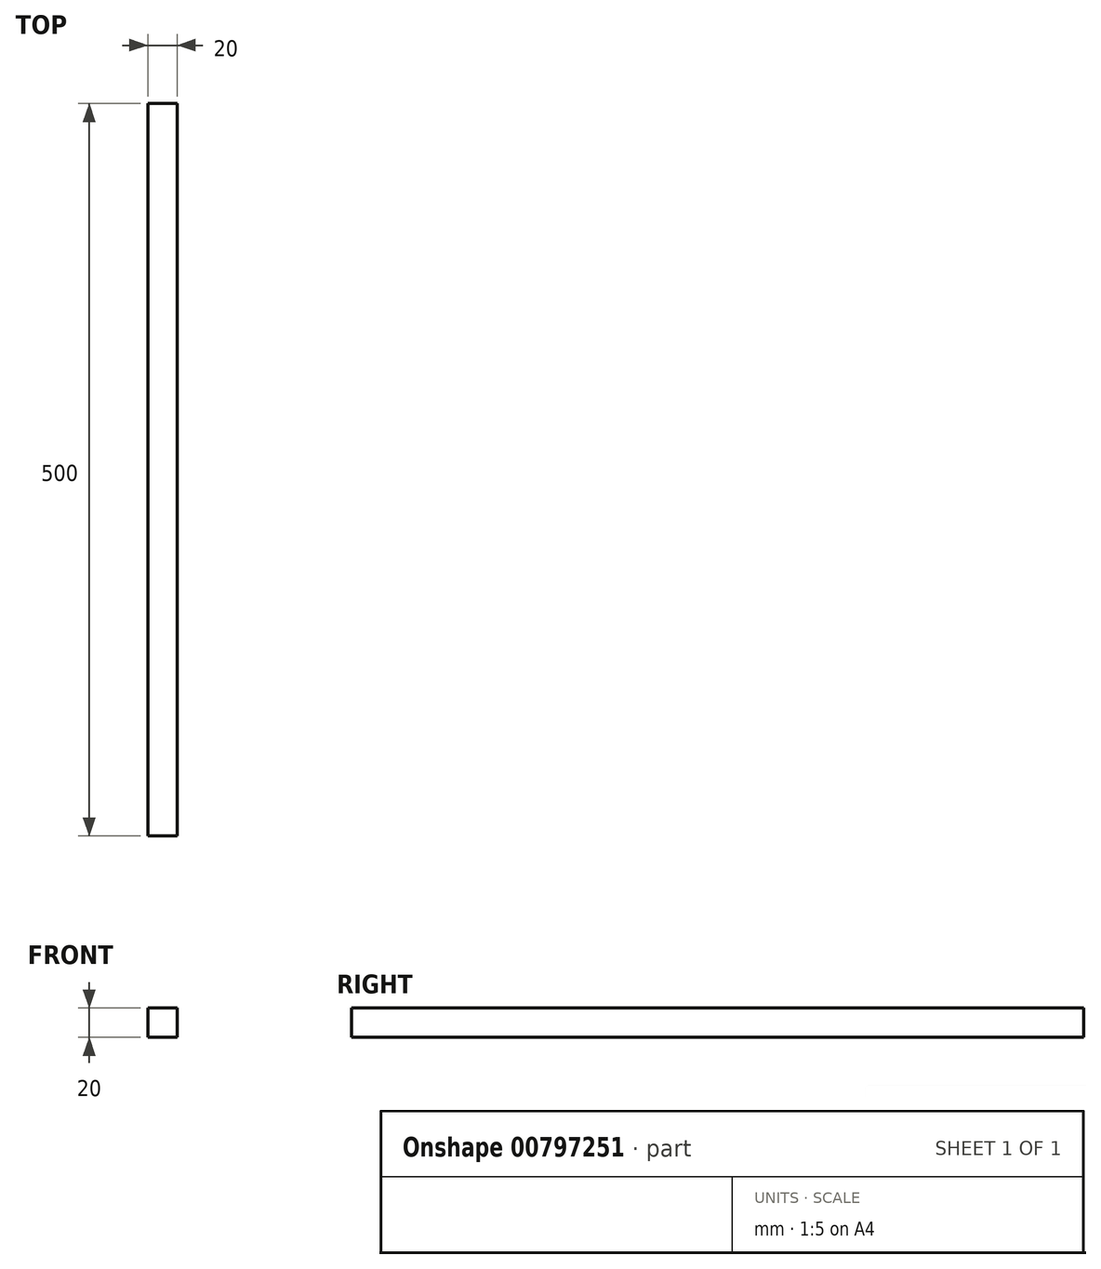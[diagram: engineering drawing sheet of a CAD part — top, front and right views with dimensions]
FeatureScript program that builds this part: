
annotation { "Feature Type Name" : "Feature", "Feature Type Description" : "" }
export const myFeature = defineFeature(function(context is Context, id is Id, definition is map)
    precondition{}
    {
        {
            var Q0;
            Q0=qCreatedBy(makeId("Front.planeOp"),FACE);
            var sketch = newSketch(context, id + "F0", { "sketchPlane" : qUnion([Q0])});
            skLineSegment(sketch, "E0.bottom", {"start": v(-68.37, 52.5) * mm, "end": v(-48.37, 52.5) * mm});
            skLineSegment(sketch, "E0.top", {"start": v(-68.37, 32.5) * mm, "end": v(-48.37, 32.5) * mm});
            skLineSegment(sketch, "E0.left", {"start": v(-68.37, 52.5) * mm, "end": v(-68.37, 32.5) * mm});
            skLineSegment(sketch, "E0.right", {"start": v(-48.37, 52.5) * mm, "end": v(-48.37, 32.5) * mm});
            skSolve(sketch);
        }
        {
            var Q0;
            Q0 = qSketchRegion(id + "F0", true);
            extrude(context, id + "F1", {"entities" : qUnion([Q0]), "depth" : 500 * mm, "offsetDistance" : 25 * mm});
        }
    });
